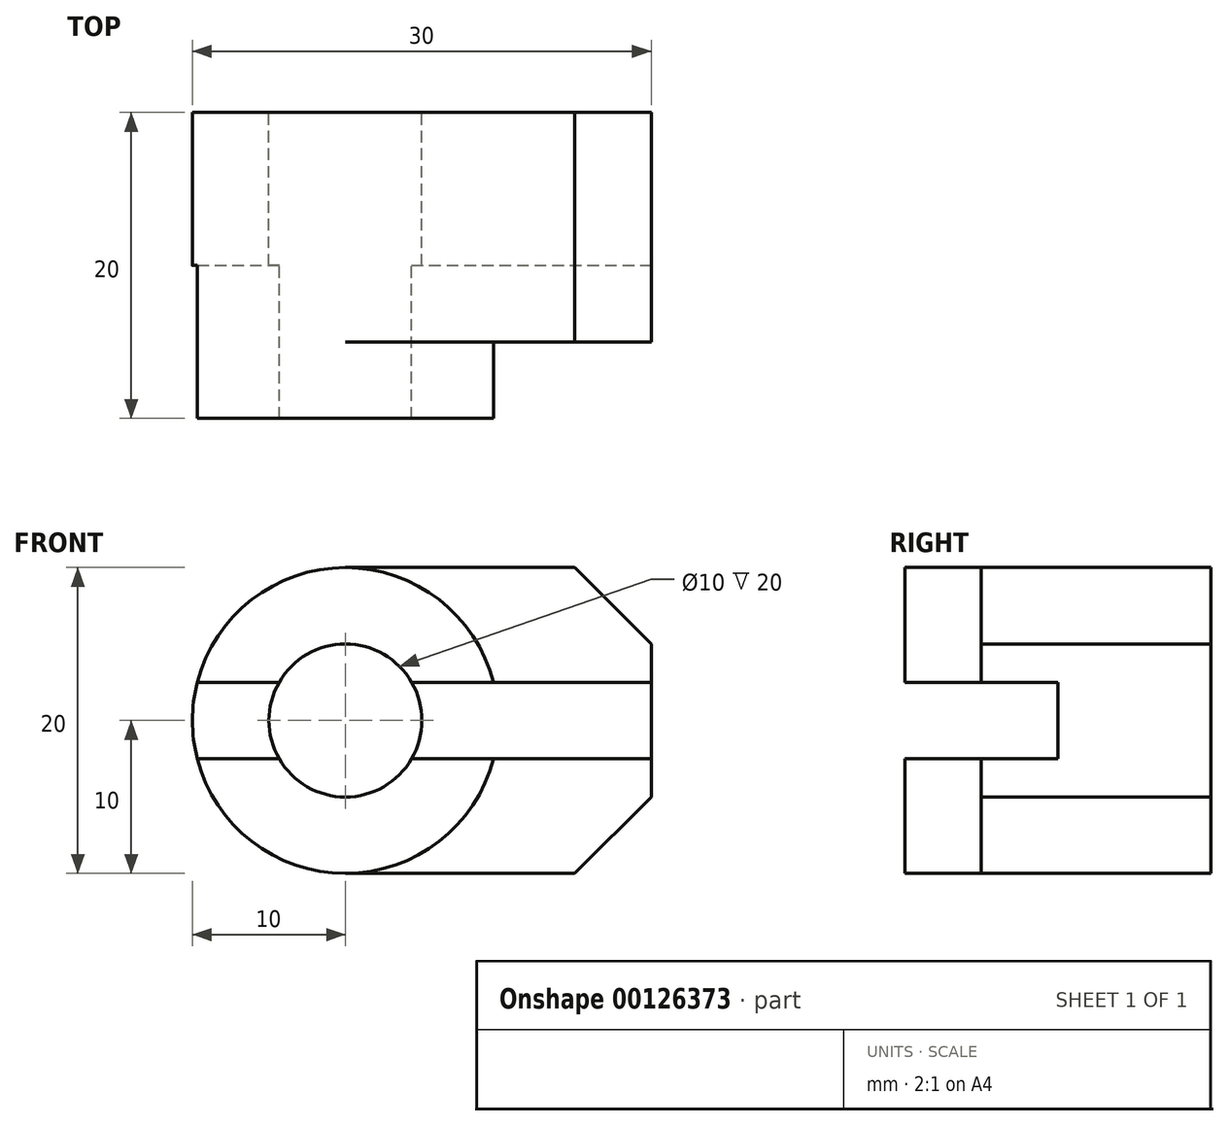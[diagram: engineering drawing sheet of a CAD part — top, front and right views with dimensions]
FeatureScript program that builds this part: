
annotation { "Feature Type Name" : "Feature", "Feature Type Description" : "" }
export const myFeature = defineFeature(function(context is Context, id is Id, definition is map)
    precondition{}
    {
        {
            var Q0;
            Q0=qCreatedBy(makeId("Front.planeOp"),FACE);
            var sketch = newSketch(context, id + "F0", { "sketchPlane" : qUnion([Q0])});
            skCircle(sketch, "E0", {"center": v(0, 0) * mm, "radius": 5 * mm});
            skCircle(sketch, "E1", {"center": v(0, 0) * mm, "radius": 10 * mm});
            skSolve(sketch);
        }
        {
            var Q0;
            Q0 = qSketchRegion(id + "F0", true);
            extrude(context, id + "F1", {"entities" : qUnion([Q0]), "depth" : 20 * mm});
        }
        {
            var Q0;
            Q0=qCreatedBy(makeId("Front.planeOp"),FACE);
            var sketch = newSketch(context, id + "F2", { "sketchPlane" : qUnion([Q0])});
            skLineSegment(sketch, "E2", {"start": v(0, 10) * mm, "end": v(15, 10) * mm});
            skLineSegment(sketch, "E3", {"start": v(15, 10) * mm, "end": v(20, 5) * mm});
            skLineSegment(sketch, "E4", {"start": v(20, 5) * mm, "end": v(20, 0) * mm});
            skLineSegment(sketch, "E5", {"start": v(20, 0) * mm, "end": v(10, 0) * mm, "construction": true});
            skLineSegment(sketch, "E6.MirrorCS", {"start": v(20, -5) * mm, "end": v(20, 0) * mm});
            skLineSegment(sketch, "E7.MirrorCS", {"start": v(15, -10) * mm, "end": v(20, -5) * mm});
            skLineSegment(sketch, "E8.MirrorCS", {"start": v(0, -10) * mm, "end": v(15, -10) * mm});
            skArc(sketch, "E9.0", {"start": v(0, -5) * mm, "mid": v(5, 0) * mm, "end": v(0, 5) * mm});
            skLineSegment(sketch, "E10", {"start": v(0, 10) * mm, "end": v(0, 5) * mm});
            skLineSegment(sketch, "E11", {"start": v(0, -5) * mm, "end": v(0, -10) * mm});
            skSolve(sketch);
        }
        {
            var Q0;
            Q0 = qSketchRegion(id + "F2", true);
            extrude(context, id + "F3", {"entities" : qUnion([Q0]), "operationType" : NewBodyOperationType.ADD, "depth" : 15 * mm});
        }
        {
            var Q0;
            Q0=makeQuery(id+"F3.opExtrude","SWEPT_FACE",FACE,{"disambiguationData":[OSD([sQuery(id+"F2.wireOp",EDGE,"E4"),sQuery(id+"F2.wireOp",EDGE,"E6.MirrorCS")])]});
            var sketch = newSketch(context, id + "F4", { "sketchPlane" : qUnion([Q0])});
            skLineSegment(sketch, "E12.bottom", {"start": v(-20, 2.5) * mm, "end": v(-10, 2.5) * mm});
            skLineSegment(sketch, "E12.top", {"start": v(-20, -2.5) * mm, "end": v(-10, -2.5) * mm});
            skLineSegment(sketch, "E12.left", {"start": v(-20, 2.5) * mm, "end": v(-20, -2.5) * mm});
            skLineSegment(sketch, "E12.right", {"start": v(-10, 2.5) * mm, "end": v(-10, -2.5) * mm});
            skSolve(sketch);
        }
        {
            var Q0;
            Q0 = qSketchRegion(id + "F4", true);
            extrude(context, id + "F5", {"entities" : qUnion([Q0]), "operationType" : NewBodyOperationType.REMOVE, "endBound" : BoundingType.THROUGH_ALL, "oppositeDirection" : true, "depth" : 25 * mm});
        }
    });
